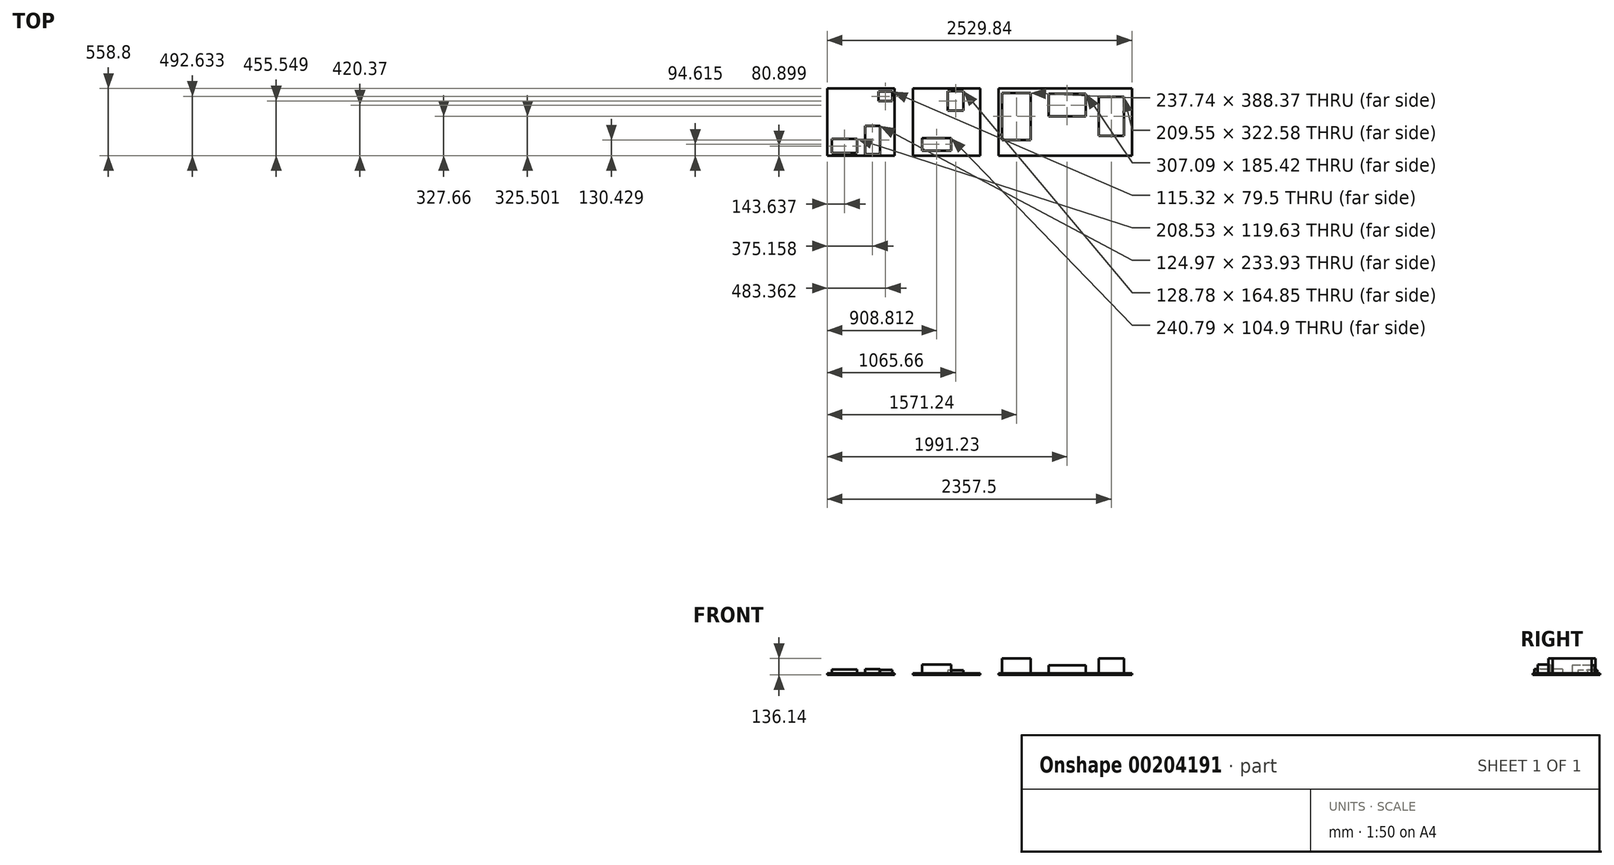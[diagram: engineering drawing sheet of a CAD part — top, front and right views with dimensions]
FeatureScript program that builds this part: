
annotation { "Feature Type Name" : "Feature", "Feature Type Description" : "" }
export const myFeature = defineFeature(function(context is Context, id is Id, definition is map)
    precondition{}
    {
        {
            var Q0;
            Q0=qCreatedBy(makeId("Top.planeOp"),FACE);
            var sketch = newSketch(context, id + "F0", { "sketchPlane" : qUnion([Q0])});
            skLineSegment(sketch, "E0.bottom", {"start": v(0, 0) * mm, "end": v(-1107.44, 0) * mm});
            skLineSegment(sketch, "E0.top", {"start": v(0, 558.8) * mm, "end": v(-1107.44, 558.8) * mm});
            skLineSegment(sketch, "E0.left", {"start": v(0, 0) * mm, "end": v(0, 558.8) * mm});
            skLineSegment(sketch, "E0.right", {"start": v(-1107.44, 0) * mm, "end": v(-1107.44, 558.8) * mm});
            skText(sketch, "E1", { "text": "Monroe", "fontName": "OpenSans-Regular.ttf"});
            skText(sketch, "E2", { "text": "Madison", "fontName": "OpenSans-Regular.ttf"});
            skText(sketch, "E3", { "text": "Main", "fontName": "OpenSans-Regular.ttf"});
            skText(sketch, "E4", { "text": "Pine", "fontName": "OpenSans-Regular.ttf"});
            skLineSegment(sketch, "E5.bottom", {"start": v(-1077.47, 519.68) * mm, "end": v(-839.72, 519.68) * mm});
            skLineSegment(sketch, "E5.top", {"start": v(-1077.47, 131.32) * mm, "end": v(-839.72, 131.32) * mm});
            skLineSegment(sketch, "E5.left", {"start": v(-1077.47, 519.68) * mm, "end": v(-1077.47, 131.32) * mm});
            skLineSegment(sketch, "E5.right", {"start": v(-839.72, 519.68) * mm, "end": v(-839.72, 131.32) * mm});
            skLineSegment(sketch, "E6.bottom", {"start": v(-277.11, 488.95) * mm, "end": v(-67.56, 488.95) * mm});
            skLineSegment(sketch, "E6.top", {"start": v(-277.11, 166.37) * mm, "end": v(-67.56, 166.37) * mm});
            skLineSegment(sketch, "E6.left", {"start": v(-277.11, 488.95) * mm, "end": v(-277.11, 166.37) * mm});
            skLineSegment(sketch, "E6.right", {"start": v(-67.56, 488.95) * mm, "end": v(-67.56, 166.37) * mm});
            skLineSegment(sketch, "E7.bottom", {"start": v(-692.15, 513.08) * mm, "end": v(-385.06, 513.08) * mm});
            skLineSegment(sketch, "E7.top", {"start": v(-692.15, 327.66) * mm, "end": v(-385.06, 327.66) * mm});
            skLineSegment(sketch, "E7.left", {"start": v(-692.15, 513.08) * mm, "end": v(-692.15, 327.66) * mm});
            skLineSegment(sketch, "E7.right", {"start": v(-385.06, 513.08) * mm, "end": v(-385.06, 327.66) * mm});
            const initialGuessF0  = {"E1": [-0.83633, -0.0677, 1, 0, 0.0508], "E2": [-0.87582, 0.62165, 1, 0, 0.0508], "E3": [0.07365, 0.20634, 0, 1, 0.0508], "E4": [-1.12846, 0.25042, 0, 1, 0.0508]};
            skSetInitialGuess(sketch, initialGuessF0);
            skSolve(sketch);
        }
        {
            var Q0;
            Q0=makeQuery(id+"F0.imprint","IMPRINT",FACE,{"disambiguationData":[TD([[makeQuery(id+"F0.imprint","IMPRINT",EDGE,{"derivedFrom":sQuery(id+"F0.wireOp",EDGE,"E0.bottom")}),-1.0]])]});
            extrude(context, id + "F1", {"entities" : qUnion([Q0]), "oppositeDirection" : true, "depth" : 12.7 * mm});
        }
        {
            var Q0;
            Q0=makeQuery(id+"F0.imprint","IMPRINT",FACE,{"disambiguationData":[TD([[makeQuery(id+"F0.imprint","IMPRINT",EDGE,{"derivedFrom":sQuery(id+"F0.wireOp",EDGE,"E5.bottom")}),-1.0]])]});
            extrude(context, id + "F2", {"entities" : qUnion([Q0]), "operationType" : NewBodyOperationType.ADD, "depth" : 123.44 * mm});
        }
        {
            var Q0;
            Q0=makeQuery(id+"F0.imprint","IMPRINT",FACE,{"disambiguationData":[TD([[makeQuery(id+"F0.imprint","IMPRINT",EDGE,{"derivedFrom":sQuery(id+"F0.wireOp",EDGE,"E6.bottom")}),-1.0]])]});
            extrude(context, id + "F3", {"entities" : qUnion([Q0]), "depth" : 123.44 * mm});
        }
        {
            var Q0;
            Q0=makeQuery(id+"F0.imprint","IMPRINT",FACE,{"disambiguationData":[TD([[makeQuery(id+"F0.imprint","IMPRINT",EDGE,{"derivedFrom":sQuery(id+"F0.wireOp",EDGE,"E7.bottom")}),-1.0]])]});
            extrude(context, id + "F4", {"entities" : qUnion([Q0]), "depth" : 65.8 * mm});
        }
        {
            var Q0;
            Q0=qCreatedBy(makeId("Top.planeOp"),FACE);
            var sketch = newSketch(context, id + "F5", { "sketchPlane" : qUnion([Q0])});
            skLineSegment(sketch, "E8.bottom", {"start": v(-1259.84, 0) * mm, "end": v(-1818.64, 0) * mm});
            skLineSegment(sketch, "E8.top", {"start": v(-1259.84, 558.8) * mm, "end": v(-1818.64, 558.8) * mm});
            skLineSegment(sketch, "E8.left", {"start": v(-1259.84, 0) * mm, "end": v(-1259.84, 558.8) * mm});
            skLineSegment(sketch, "E8.right", {"start": v(-1818.64, 0) * mm, "end": v(-1818.64, 558.8) * mm});
            skLineSegment(sketch, "E9.bottom", {"start": v(-1399.8, 537.97) * mm, "end": v(-1528.57, 537.97) * mm});
            skLineSegment(sketch, "E9.top", {"start": v(-1399.8, 373.13) * mm, "end": v(-1528.57, 373.13) * mm});
            skLineSegment(sketch, "E9.left", {"start": v(-1399.8, 537.97) * mm, "end": v(-1399.8, 373.13) * mm});
            skLineSegment(sketch, "E9.right", {"start": v(-1528.57, 537.97) * mm, "end": v(-1528.57, 373.13) * mm});
            skText(sketch, "E10", { "text": "Cherry", "fontName": "OpenSans-Regular.ttf"});
            skLineSegment(sketch, "E11.bottom", {"start": v(-1741.42, 42.16) * mm, "end": v(-1500.63, 42.16) * mm});
            skLineSegment(sketch, "E11.top", {"start": v(-1741.42, 147.07) * mm, "end": v(-1500.63, 147.07) * mm});
            skLineSegment(sketch, "E11.left", {"start": v(-1741.42, 42.16) * mm, "end": v(-1741.42, 147.07) * mm});
            skLineSegment(sketch, "E11.right", {"start": v(-1500.63, 42.16) * mm, "end": v(-1500.63, 147.07) * mm});
            const initialGuessF5  = {"E10": [-1.85414, 0.17973, 0, 1, 0.05955]};
            skSetInitialGuess(sketch, initialGuessF5);
            skSolve(sketch);
        }
        {
            var Q0;
            Q0=makeQuery(id+"F5.imprint","IMPRINT",FACE,{"disambiguationData":[TD([[makeQuery(id+"F5.imprint","IMPRINT",EDGE,{"derivedFrom":sQuery(id+"F5.wireOp",EDGE,"E8.bottom")}),-1.0]])]});
            extrude(context, id + "F6", {"entities" : qUnion([Q0]), "oppositeDirection" : true, "depth" : 12.7 * mm});
        }
        {
            var Q0;
            Q0=makeQuery(id+"F5.imprint","IMPRINT",FACE,{"disambiguationData":[TD([[makeQuery(id+"F5.imprint","IMPRINT",EDGE,{"derivedFrom":sQuery(id+"F5.wireOp",EDGE,"E9.bottom")}),1.0]])]});
            extrude(context, id + "F7", {"entities" : qUnion([Q0]), "depth" : 25.4 * mm});
        }
        {
            var Q0;
            Q0=makeQuery(id+"F5.imprint","IMPRINT",FACE,{"disambiguationData":[TD([[makeQuery(id+"F5.imprint","IMPRINT",EDGE,{"derivedFrom":sQuery(id+"F5.wireOp",EDGE,"E11.bottom")}),1.0]])]});
            extrude(context, id + "F8", {"entities" : qUnion([Q0]), "depth" : 71.63 * mm});
        }
        {
            var Q0;
            Q0=qCreatedBy(makeId("Top.planeOp"),FACE);
            var sketch = newSketch(context, id + "F9", { "sketchPlane" : qUnion([Q0])});
            skLineSegment(sketch, "E12.bottom", {"start": v(-1971.04, 0) * mm, "end": v(-2529.84, 0) * mm});
            skLineSegment(sketch, "E12.top", {"start": v(-1971.04, 558.8) * mm, "end": v(-2529.84, 558.8) * mm});
            skLineSegment(sketch, "E12.left", {"start": v(-1971.04, 0) * mm, "end": v(-1971.04, 558.8) * mm});
            skLineSegment(sketch, "E12.right", {"start": v(-2529.84, 0) * mm, "end": v(-2529.84, 558.8) * mm});
            skText(sketch, "E13", { "text": "Walnut", "fontName": "OpenSans-Regular.ttf"});
            skLineSegment(sketch, "E14.bottom", {"start": v(-2092.2, 247.4) * mm, "end": v(-2217.17, 247.4) * mm});
            skLineSegment(sketch, "E14.top", {"start": v(-2092.2, 13.46) * mm, "end": v(-2217.17, 13.46) * mm});
            skLineSegment(sketch, "E14.left", {"start": v(-2092.2, 247.4) * mm, "end": v(-2092.2, 13.46) * mm});
            skLineSegment(sketch, "E14.right", {"start": v(-2217.17, 247.4) * mm, "end": v(-2217.17, 13.46) * mm});
            skLineSegment(sketch, "E15.bottom", {"start": v(-2281.94, 140.72) * mm, "end": v(-2490.47, 140.72) * mm});
            skLineSegment(sketch, "E15.top", {"start": v(-2281.94, 21.08) * mm, "end": v(-2490.47, 21.08) * mm});
            skLineSegment(sketch, "E15.left", {"start": v(-2281.94, 140.72) * mm, "end": v(-2281.94, 21.08) * mm});
            skLineSegment(sketch, "E15.right", {"start": v(-2490.47, 140.72) * mm, "end": v(-2490.47, 21.08) * mm});
            skLineSegment(sketch, "E16.bottom", {"start": v(-1988.82, 532.38) * mm, "end": v(-2104.14, 532.38) * mm});
            skLineSegment(sketch, "E16.top", {"start": v(-1988.82, 452.88) * mm, "end": v(-2104.14, 452.88) * mm});
            skLineSegment(sketch, "E16.left", {"start": v(-1988.82, 532.38) * mm, "end": v(-1988.82, 452.88) * mm});
            skLineSegment(sketch, "E16.right", {"start": v(-2104.14, 532.38) * mm, "end": v(-2104.14, 452.88) * mm});
            const initialGuessF9  = {"E13": [-2.58064, 0.1524, 0, 1, 0.0762]};
            skSetInitialGuess(sketch, initialGuessF9);
            skSolve(sketch);
        }
        {
            var Q0;
            Q0=makeQuery(id+"F9.imprint","IMPRINT",FACE,{"disambiguationData":[TD([[makeQuery(id+"F9.imprint","IMPRINT",EDGE,{"derivedFrom":sQuery(id+"F9.wireOp",EDGE,"E12.bottom")}),-1.0]])]});
            extrude(context, id + "F10", {"entities" : qUnion([Q0]), "oppositeDirection" : true, "depth" : 12.7 * mm});
        }
        {
            var Q0;
            Q0=makeQuery(id+"F9.imprint","IMPRINT",FACE,{"disambiguationData":[TD([[makeQuery(id+"F9.imprint","IMPRINT",EDGE,{"derivedFrom":sQuery(id+"F9.wireOp",EDGE,"E15.bottom")}),1.0]])]});
            extrude(context, id + "F11", {"entities" : qUnion([Q0]), "depth" : 31.5 * mm});
        }
        {
            var Q0;
            Q0=makeQuery(id+"F9.imprint","IMPRINT",FACE,{"disambiguationData":[TD([[makeQuery(id+"F9.imprint","IMPRINT",EDGE,{"derivedFrom":sQuery(id+"F9.wireOp",EDGE,"E14.bottom")}),1.0]])]});
            extrude(context, id + "F12", {"entities" : qUnion([Q0]), "depth" : 33.27 * mm});
        }
        {
            var Q0;
            Q0=makeQuery(id+"F9.imprint","IMPRINT",FACE,{"disambiguationData":[TD([[makeQuery(id+"F9.imprint","IMPRINT",EDGE,{"derivedFrom":sQuery(id+"F9.wireOp",EDGE,"E16.bottom")}),1.0]])]});
            extrude(context, id + "F13", {"entities" : qUnion([Q0]), "depth" : 29.2 * mm});
        }
    });
